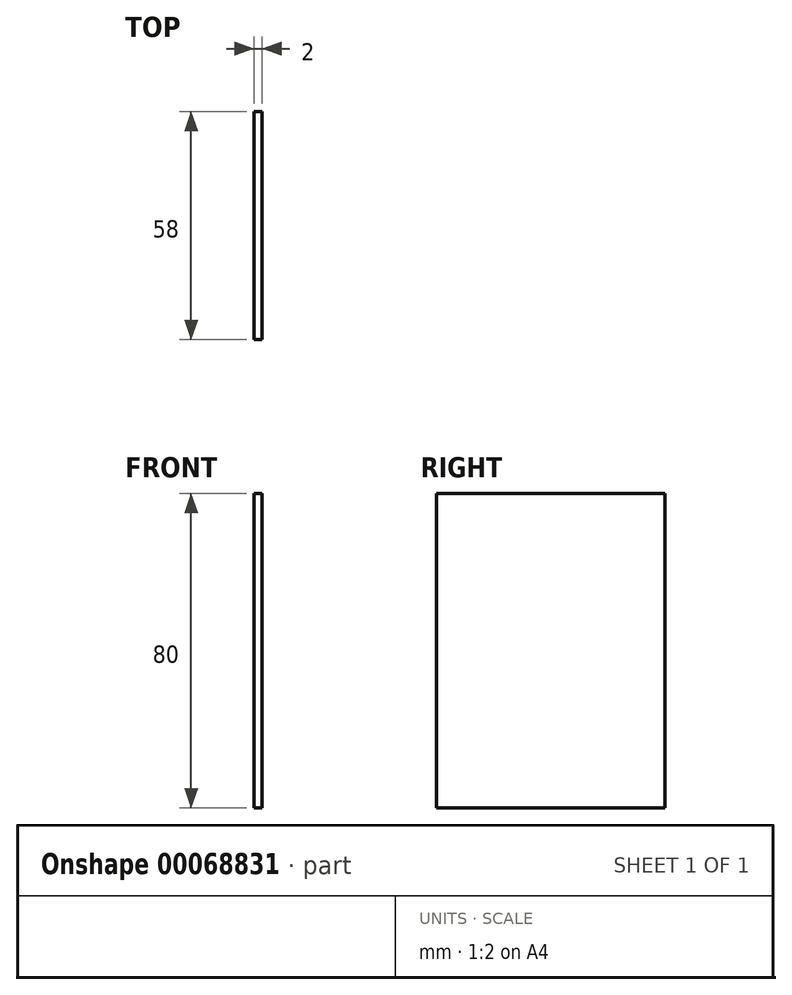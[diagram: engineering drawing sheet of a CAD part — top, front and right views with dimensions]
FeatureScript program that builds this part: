
annotation { "Feature Type Name" : "Feature", "Feature Type Description" : "" }
export const myFeature = defineFeature(function(context is Context, id is Id, definition is map)
    precondition{}
    {
        {
            var Q0;
            Q0=qCreatedBy(makeId("Right.planeOp"),FACE);
            var sketch = newSketch(context, id + "F0", { "sketchPlane" : qUnion([Q0])});
            skLineSegment(sketch, "E0.bottom", {"start": v(0, 0) * mm, "end": v(58, 0) * mm});
            skLineSegment(sketch, "E0.top", {"start": v(0, 80) * mm, "end": v(58, 80) * mm});
            skLineSegment(sketch, "E0.left", {"start": v(0, 0) * mm, "end": v(0, 80) * mm});
            skLineSegment(sketch, "E0.right", {"start": v(58, 0) * mm, "end": v(58, 80) * mm});
            skSolve(sketch);
        }
        {
            var Q0;
            Q0 = qSketchRegion(id + "F0", true);
            extrude(context, id + "F1", {"entities" : qUnion([Q0]), "depth" : 2 * mm});
        }
    });
